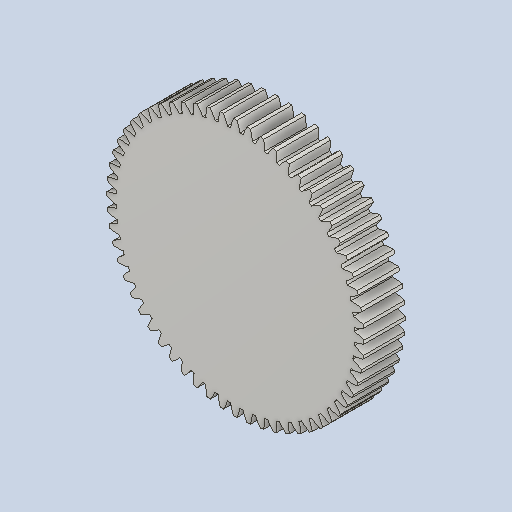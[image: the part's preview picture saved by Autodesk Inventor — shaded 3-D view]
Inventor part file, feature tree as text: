
AUTODESK INVENTOR PART (.ipt)
format: ipt  version: 2022 (Build 260153000, 153)  size: 390,656 bytes
history: native  units: mm (DEFAULTED — no unit token found)
features: plane x3, other x3, sketch x2, extrude x1
ambient origin geometry x8: Origin, YZ Plane, XZ Plane, XY Plane, X Axis, Y Axis, Z Axis, Center Point
bodies: Solid1 (feature_tree)
feature tree (9):
  extrude  "Extrusion1"  Depth=25.4mm TaperAngle=0.0deg
  plane  "Work Plane1"
  plane  "Work Plane2"
  plane  "Work Plane3"
  other  "Spur Gear"
  sketch  "Sketch1"  dims[d0=157.48mm d1=25.4mm d2=0.0mm]
  sketch  "Sketch2"  dims[d3=152.4mm d4=76.2mm d5=0.0mm d6=0.0mm d7=0.523599mm d9=0.0mm d14=0.0mm d15=101.6mm d16=0.0mm d17=0.0mm d18=0.0mm d19=101.6mm]
  other  "Srf1"
  other  "Pitch Diameter"
